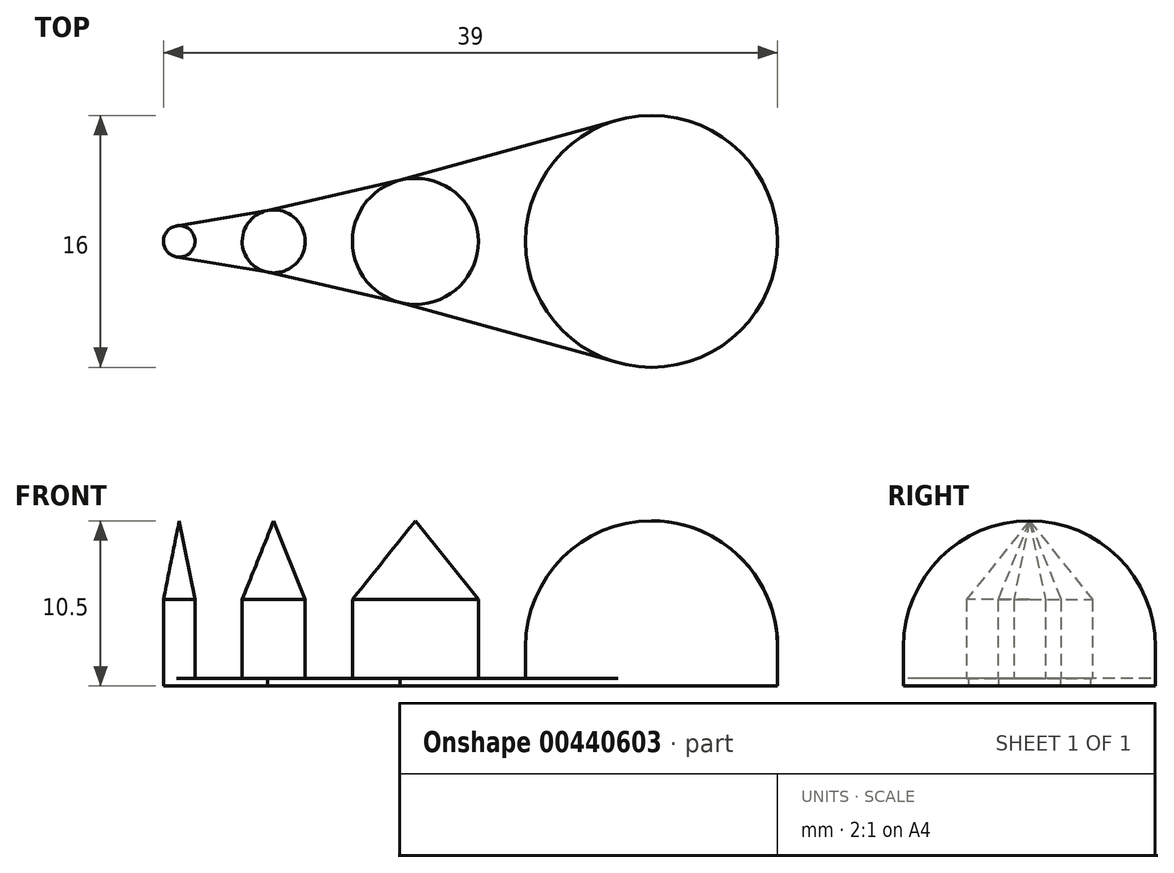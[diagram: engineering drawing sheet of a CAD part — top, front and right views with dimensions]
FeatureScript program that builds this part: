
annotation { "Feature Type Name" : "Feature", "Feature Type Description" : "" }
export const myFeature = defineFeature(function(context is Context, id is Id, definition is map)
    precondition{}
    {
        {
            var Q0;
            Q0=qCreatedBy(makeId("Top.planeOp"),FACE);
            var sketch = newSketch(context, id + "F0", { "sketchPlane" : qUnion([Q0])});
            skCircle(sketch, "E0", {"center": v(30.82, 0) * mm, "radius": 8 * mm});
            skCircle(sketch, "E1", {"center": v(15.82, 0) * mm, "radius": 4 * mm, "construction": true});
            skCircle(sketch, "E2", {"center": v(6.82, 0) * mm, "radius": 2 * mm, "construction": true});
            skCircle(sketch, "E3", {"center": v(0.82, 0) * mm, "radius": 1 * mm});
            skLineSegment(sketch, "E4", {"start": v(1.82, 0) * mm, "end": v(4.82, 0) * mm, "construction": true});
            skLineSegment(sketch, "E5", {"start": v(8.82, 0) * mm, "end": v(11.82, 0) * mm, "construction": true});
            skLineSegment(sketch, "E6", {"start": v(19.82, 0) * mm, "end": v(22.82, 0) * mm, "construction": true});
            skLineSegment(sketch, "E7", {"start": v(0.65, -0.99) * mm, "end": v(6.48, -1.97) * mm});
            skLineSegment(sketch, "E8", {"start": v(6.37, -1.95) * mm, "end": v(14.93, -3.9) * mm});
            skLineSegment(sketch, "E9", {"start": v(14.75, -3.86) * mm, "end": v(28.68, -7.71) * mm});
            skLineSegment(sketch, "E10", {"start": v(28.68, 7.71) * mm, "end": v(14.75, 3.86) * mm});
            skLineSegment(sketch, "E11", {"start": v(14.93, 3.9) * mm, "end": v(6.37, 1.95) * mm});
            skLineSegment(sketch, "E12", {"start": v(6.48, 1.97) * mm, "end": v(0.65, 0.99) * mm});
            skSolve(sketch);
        }
        {
            var Q0;
            Q0 = qSketchRegion(id + "F0", true);
            extrude(context, id + "F1", {"entities" : qUnion([Q0]), "depth" : 0.5 * mm});
        }
        {
            var Q0;
            Q0=makeQuery(id+"F1.opExtrude","CAP_FACE",FACE,{"disambiguationData":[OSD([sQuery(id+"F0.wireOp",EDGE,"E0"),sQuery(id+"F0.wireOp",EDGE,"E3"),sQuery(id+"F0.wireOp",EDGE,"E7"),sQuery(id+"F0.wireOp",EDGE,"E8"),sQuery(id+"F0.wireOp",EDGE,"E9"),sQuery(id+"F0.wireOp",EDGE,"E10"),sQuery(id+"F0.wireOp",EDGE,"E11"),sQuery(id+"F0.wireOp",EDGE,"E12")])],"isStart":false});
            var sketch = newSketch(context, id + "F2", { "sketchPlane" : qUnion([Q0])});
            skCircle(sketch, "E13", {"center": v(6.82, 0) * mm, "radius": 2 * mm});
            skCircle(sketch, "E14", {"center": v(0.82, 0) * mm, "radius": 1 * mm});
            skCircle(sketch, "E15", {"center": v(15.82, 0) * mm, "radius": 4 * mm});
            skCircle(sketch, "E16", {"center": v(30.82, 0) * mm, "radius": 8 * mm});
            skSolve(sketch);
        }
        {
            var Q0;
            Q0 = qSketchRegion(id + "F2", true);
            extrude(context, id + "F3", {"entities" : qUnion([Q0]), "operationType" : NewBodyOperationType.ADD, "depth" : 10 * mm});
        }
        {
            var Q0;
            Q0=makeQuery(id+"F3.opExtrude","CAP_EDGE",EDGE,{"disambiguationData":[OSD([sQuery(id+"F2.wireOp",EDGE,"E14")])],"isStart":false});
            chamfer(context, id + "F4", {"entities" : qUnion([Q0]), "chamferType" : ChamferType.TWO_OFFSETS, "width1" : 1 * mm, "oppositeDirection" : false, "width2" : 5 * mm, "tangentPropagation" : true});
        }
        {
            var Q0;
            Q0=makeQuery(id+"F3.opExtrude","CAP_EDGE",EDGE,{"disambiguationData":[OSD([sQuery(id+"F2.wireOp",EDGE,"E16")])],"isStart":false});
            fillet(context, id + "F5", {"entities" : qUnion([Q0]), "radius" : 8 * mm, "tangentPropagation" : true, "allowEdgeOverflow" : false});
        }
        {
            var Q0;
            Q0=makeQuery(id+"F3.opExtrude","CAP_EDGE",EDGE,{"disambiguationData":[OSD([sQuery(id+"F2.wireOp",EDGE,"E13")])],"isStart":false});
            chamfer(context, id + "F6", {"entities" : qUnion([Q0]), "chamferType" : ChamferType.TWO_OFFSETS, "width1" : 2 * mm, "oppositeDirection" : false, "width2" : 5 * mm, "tangentPropagation" : true});
        }
        {
            var Q0;
            Q0=makeQuery(id+"F3.opExtrude","CAP_EDGE",EDGE,{"disambiguationData":[OSD([sQuery(id+"F2.wireOp",EDGE,"E15")])],"isStart":false});
            chamfer(context, id + "F7", {"entities" : qUnion([Q0]), "chamferType" : ChamferType.TWO_OFFSETS, "width1" : 4 * mm, "oppositeDirection" : false, "width2" : 5 * mm, "tangentPropagation" : true});
        }
    });
